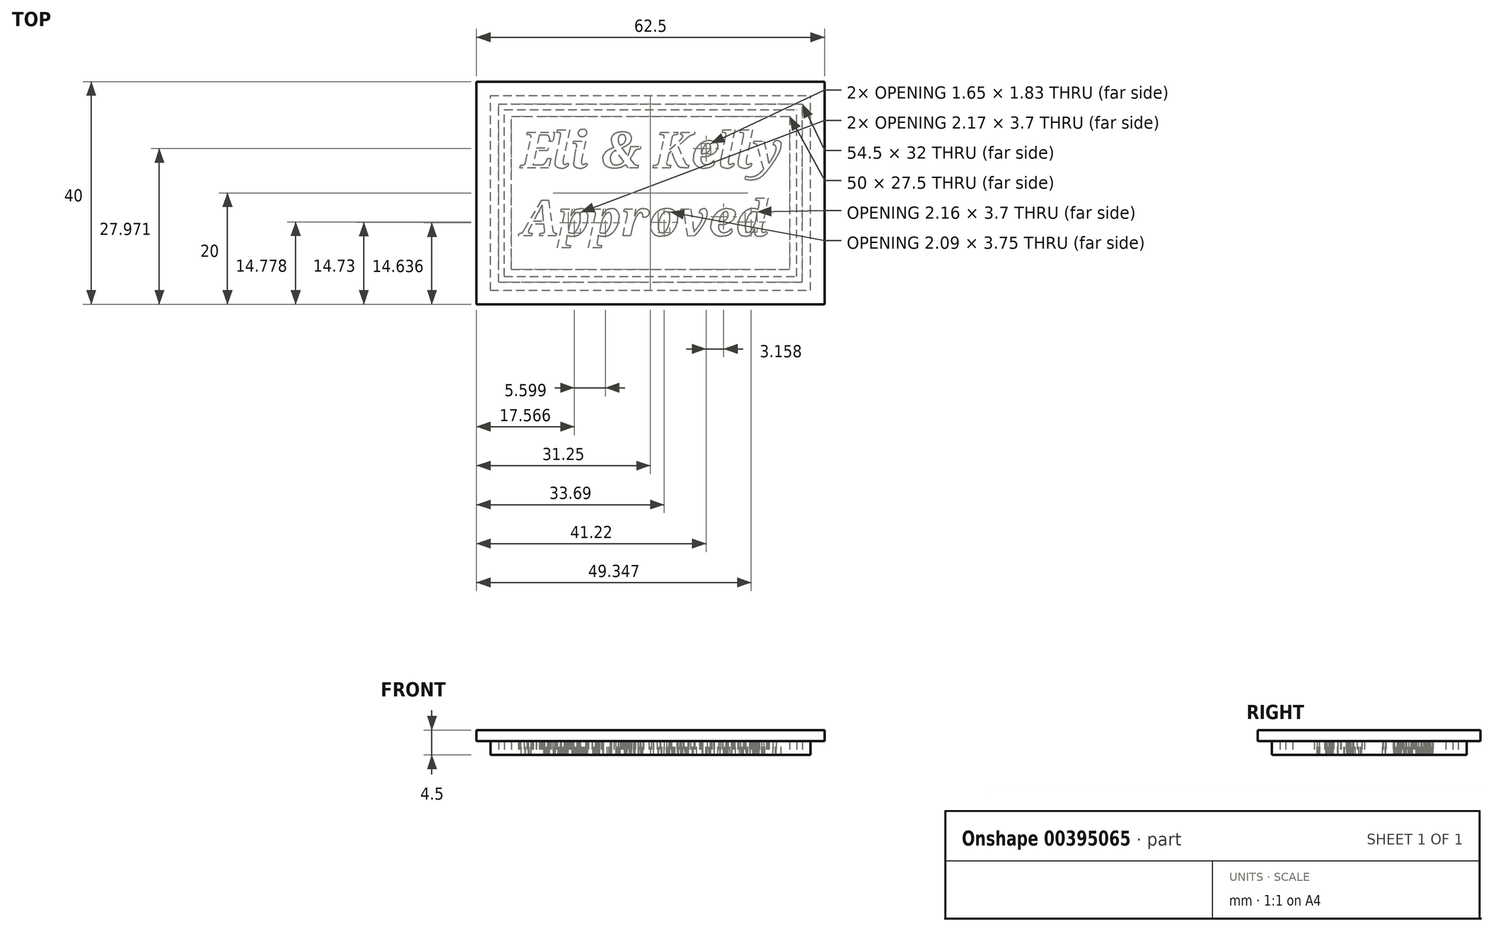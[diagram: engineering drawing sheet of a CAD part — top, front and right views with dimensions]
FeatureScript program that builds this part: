
annotation { "Feature Type Name" : "Feature", "Feature Type Description" : "" }
export const myFeature = defineFeature(function(context is Context, id is Id, definition is map)
    precondition{}
    {
        {
            var Q0;
            Q0=qCreatedBy(makeId("Top.planeOp"),FACE);
            var sketch = newSketch(context, id + "F0", { "sketchPlane" : qUnion([Q0])});
            skLineSegment(sketch, "E0.bottom", {"start": v(-28.75, -17.5) * mm, "end": v(28.75, -17.5) * mm});
            skLineSegment(sketch, "E0.top", {"start": v(-28.75, 17.5) * mm, "end": v(28.75, 17.5) * mm});
            skLineSegment(sketch, "E0.left", {"start": v(-28.75, -17.5) * mm, "end": v(-28.75, 17.5) * mm});
            skLineSegment(sketch, "E0.right", {"start": v(28.75, -17.5) * mm, "end": v(28.75, 17.5) * mm});
            skPoint(sketch, "E0.middle", {"position": v(0, 0) * mm});
            skLineSegment(sketch, "E1.bottom", {"start": v(-25, -13.75) * mm, "end": v(25, -13.75) * mm});
            skLineSegment(sketch, "E1.top", {"start": v(-25, 13.75) * mm, "end": v(25, 13.75) * mm});
            skLineSegment(sketch, "E1.left", {"start": v(-25, -13.75) * mm, "end": v(-25, 13.75) * mm});
            skLineSegment(sketch, "E2", {"start": v(25, 13.75) * mm, "end": v(25, -13.75) * mm});
            skText(sketch, "E3", { "text": "Eli & Kelly\nApproved", "fontName": "NotoSerif-BoldItalic.ttf"});
            skLineSegment(sketch, "E4.bottom", {"start": v(-27.25, -16) * mm, "end": v(27.25, -16) * mm});
            skLineSegment(sketch, "E4.top", {"start": v(-27.25, 16) * mm, "end": v(27.25, 16) * mm});
            skLineSegment(sketch, "E4.left", {"start": v(-27.25, -16) * mm, "end": v(-27.25, 16) * mm});
            skLineSegment(sketch, "E4.right", {"start": v(27.25, -16) * mm, "end": v(27.25, 16) * mm});
            skLineSegment(sketch, "E5.bottom", {"start": v(-26.25, -15) * mm, "end": v(26.25, -15) * mm});
            skLineSegment(sketch, "E5.top", {"start": v(-26.25, 15) * mm, "end": v(26.25, 15) * mm});
            skLineSegment(sketch, "E5.left", {"start": v(-26.25, -15) * mm, "end": v(-26.25, 15) * mm});
            skLineSegment(sketch, "E5.right", {"start": v(26.25, -15) * mm, "end": v(26.25, 15) * mm});
            const initialGuessF0  = {"E3": [-0.02325, 0.00452, 1, 0, 0.00647]};
            skSetInitialGuess(sketch, initialGuessF0);
            skSolve(sketch);
        }
        {
            var Q0;
            Q0=makeQuery(id+"F0.imprint","IMPRINT",FACE,{"disambiguationData":[TD([[makeQuery(id+"F0.imprint","IMPRINT",EDGE,{"derivedFrom":sQuery(id+"F0.wireOp",EDGE,"E3.sketch_text.stroke-423")}),-1.0]])]});
            var Q1;
            Q1=makeQuery(id+"F0.imprint","IMPRINT",FACE,{"disambiguationData":[TD([[makeQuery(id+"F0.imprint","IMPRINT",EDGE,{"derivedFrom":sQuery(id+"F0.wireOp",EDGE,"E3.sketch_text.stroke-489")}),-1.0]])]});
            var Q2;
            Q2=makeQuery(id+"F0.imprint","IMPRINT",FACE,{"disambiguationData":[TD([[makeQuery(id+"F0.imprint","IMPRINT",EDGE,{"derivedFrom":sQuery(id+"F0.wireOp",EDGE,"E3.sketch_text.stroke-555")}),-1.0]])]});
            var Q3;
            Q3=makeQuery(id+"F0.imprint","IMPRINT",FACE,{"disambiguationData":[TD([[makeQuery(id+"F0.imprint","IMPRINT",EDGE,{"derivedFrom":sQuery(id+"F0.wireOp",EDGE,"E3.sketch_text.stroke-585")}),-1.0]])]});
            var Q4;
            Q4=makeQuery(id+"F0.imprint","IMPRINT",FACE,{"disambiguationData":[TD([[makeQuery(id+"F0.imprint","IMPRINT",EDGE,{"derivedFrom":sQuery(id+"F0.wireOp",EDGE,"E3.sketch_text.stroke-621")}),-1.0]])]});
            var Q5;
            Q5=makeQuery(id+"F0.imprint","IMPRINT",FACE,{"disambiguationData":[TD([[makeQuery(id+"F0.imprint","IMPRINT",EDGE,{"derivedFrom":sQuery(id+"F0.wireOp",EDGE,"E3.sketch_text.stroke-652")}),-1.0]])]});
            var Q6;
            Q6=makeQuery(id+"F0.imprint","IMPRINT",FACE,{"disambiguationData":[TD([[makeQuery(id+"F0.imprint","IMPRINT",EDGE,{"derivedFrom":sQuery(id+"F0.wireOp",EDGE,"E3.sketch_text.stroke-695")}),-1.0]])]});
            var Q7;
            Q7=makeQuery(id+"F0.imprint","IMPRINT",FACE,{"disambiguationData":[TD([[makeQuery(id+"F0.imprint","IMPRINT",EDGE,{"derivedFrom":sQuery(id+"F0.wireOp",EDGE,"E3.sketch_text.stroke-0")}),-1.0]])]});
            var Q8;
            Q8=makeQuery(id+"F0.imprint","IMPRINT",FACE,{"disambiguationData":[TD([[makeQuery(id+"F0.imprint","IMPRINT",EDGE,{"derivedFrom":sQuery(id+"F0.wireOp",EDGE,"E3.sketch_text.stroke-380")}),-1.0]])]});
            var Q9;
            Q9=makeQuery(id+"F0.imprint","IMPRINT",FACE,{"disambiguationData":[TD([[makeQuery(id+"F0.imprint","IMPRINT",EDGE,{"derivedFrom":sQuery(id+"F0.wireOp",EDGE,"E3.sketch_text.stroke-41")}),-1.0]])]});
            var Q10;
            Q10=makeQuery(id+"F0.imprint","IMPRINT",FACE,{"disambiguationData":[TD([[makeQuery(id+"F0.imprint","IMPRINT",EDGE,{"derivedFrom":sQuery(id+"F0.wireOp",EDGE,"E3.sketch_text.stroke-68")}),-1.0]])]});
            var Q11;
            Q11=makeQuery(id+"F0.imprint","IMPRINT",FACE,{"disambiguationData":[TD([[makeQuery(id+"F0.imprint","IMPRINT",EDGE,{"derivedFrom":sQuery(id+"F0.wireOp",EDGE,"E3.sketch_text.stroke-96")}),-1.0]])]});
            var Q12;
            Q12=makeQuery(id+"F0.imprint","IMPRINT",FACE,{"disambiguationData":[TD([[makeQuery(id+"F0.imprint","IMPRINT",EDGE,{"derivedFrom":sQuery(id+"F0.wireOp",EDGE,"E3.sketch_text.stroke-112")}),-1.0]])]});
            var Q13;
            Q13=makeQuery(id+"F0.imprint","IMPRINT",FACE,{"disambiguationData":[TD([[makeQuery(id+"F0.imprint","IMPRINT",EDGE,{"derivedFrom":sQuery(id+"F0.wireOp",EDGE,"E3.sketch_text.stroke-179")}),-1.0]])]});
            var Q14;
            Q14=makeQuery(id+"F0.imprint","IMPRINT",FACE,{"disambiguationData":[TD([[makeQuery(id+"F0.imprint","IMPRINT",EDGE,{"derivedFrom":sQuery(id+"F0.wireOp",EDGE,"E3.sketch_text.stroke-240")}),-1.0]])]});
            var Q15;
            Q15=makeQuery(id+"F0.imprint","IMPRINT",FACE,{"disambiguationData":[TD([[makeQuery(id+"F0.imprint","IMPRINT",EDGE,{"derivedFrom":sQuery(id+"F0.wireOp",EDGE,"E3.sketch_text.stroke-283")}),-1.0]])]});
            var Q16;
            Q16=makeQuery(id+"F0.imprint","IMPRINT",FACE,{"disambiguationData":[TD([[makeQuery(id+"F0.imprint","IMPRINT",EDGE,{"derivedFrom":sQuery(id+"F0.wireOp",EDGE,"E3.sketch_text.stroke-310")}),-1.0]])]});
            var Q17;
            Q17=makeQuery(id+"F0.imprint","IMPRINT",FACE,{"disambiguationData":[TD([[makeQuery(id+"F0.imprint","IMPRINT",EDGE,{"derivedFrom":sQuery(id+"F0.wireOp",EDGE,"E3.sketch_text.stroke-337")}),-1.0]])]});
            var Q18;
            Q18=makeQuery(id+"F0.imprint","IMPRINT",FACE,{"disambiguationData":[TD([[makeQuery(id+"F0.imprint","IMPRINT",EDGE,{"derivedFrom":sQuery(id+"F0.wireOp",EDGE,"E0.bottom")}),1.0]])]});
            var Q19;
            Q19=makeQuery(id+"F0.imprint","IMPRINT",FACE,{"disambiguationData":[TD([[makeQuery(id+"F0.imprint","IMPRINT",EDGE,{"derivedFrom":sQuery(id+"F0.wireOp",EDGE,"E1.bottom")}),-1.0]])]});
            extrude(context, id + "F1", {"entities" : qUnion([Q0, Q1, Q2, Q3, Q4, Q5, Q6, Q7, Q8, Q9, Q10, Q11, Q12, Q13, Q14, Q15, Q16, Q17, Q18, Q19]), "depth" : 2.5 * mm});
        }
        {
            var Q0;
            Q0=makeQuery(id+"F1.opExtrude","CAP_FACE",FACE,{"disambiguationData":[OSD([sQuery(id+"F0.wireOp",EDGE,"E0.bottom"),sQuery(id+"F0.wireOp",EDGE,"E0.top"),sQuery(id+"F0.wireOp",EDGE,"E0.left"),sQuery(id+"F0.wireOp",EDGE,"E0.right"),sQuery(id+"F0.wireOp",EDGE,"E4.bottom"),sQuery(id+"F0.wireOp",EDGE,"E4.top"),sQuery(id+"F0.wireOp",EDGE,"E4.left"),sQuery(id+"F0.wireOp",EDGE,"E4.right")])],"isStart":false});
            var sketch = newSketch(context, id + "F2", { "sketchPlane" : qUnion([Q0])});
            skLineSegment(sketch, "E6.bottom", {"start": v(-31.25, -20) * mm, "end": v(31.25, -20) * mm});
            skLineSegment(sketch, "E6.top", {"start": v(-31.25, 20) * mm, "end": v(31.25, 20) * mm});
            skLineSegment(sketch, "E6.left", {"start": v(-31.25, -20) * mm, "end": v(-31.25, 20) * mm});
            skLineSegment(sketch, "E6.right", {"start": v(31.25, -20) * mm, "end": v(31.25, 20) * mm});
            skPoint(sketch, "E6.middle", {"position": v(0, 0) * mm});
            skLineSegment(sketch, "E7.bottom", {"start": v(-28.75, -17.5) * mm, "end": v(28.75, -17.5) * mm});
            skLineSegment(sketch, "E7.top", {"start": v(-28.75, 17.5) * mm, "end": v(28.75, 17.5) * mm});
            skLineSegment(sketch, "E7.left", {"start": v(-28.75, -17.5) * mm, "end": v(-28.75, 17.5) * mm});
            skLineSegment(sketch, "E7.right", {"start": v(28.75, -17.5) * mm, "end": v(28.75, 17.5) * mm});
            skSolve(sketch);
        }
        {
            var Q0;
            Q0 = qSketchRegion(id + "F2", true);
            var Q1;
            Q1=makeQuery(id+"F2.imprint","IMPRINT",FACE,{"disambiguationData":[TD([[makeQuery(id+"F2.imprint","IMPRINT",EDGE,{"derivedFrom":sQuery(id+"F2.wireOp",EDGE,"E7.bottom")}),1.0]])]});
            var Q2;
            Q2=makeQuery(id+"F2.imprint","IMPRINT",FACE,{"disambiguationData":[TD([[makeQuery(id+"F2.imprint","IMPRINT",EDGE,{"derivedFrom":makeQuery(id+"F1.opExtrude","CAP_EDGE",EDGE,{"disambiguationData":[OSD([sQuery(id+"F0.wireOp",EDGE,"E4.bottom")])],"isStart":false})}),1.0]])]});
            extrude(context, id + "F3", {"entities" : qUnion([Q0, Q1, Q2]), "depth" : 2 * mm});
        }
    });
